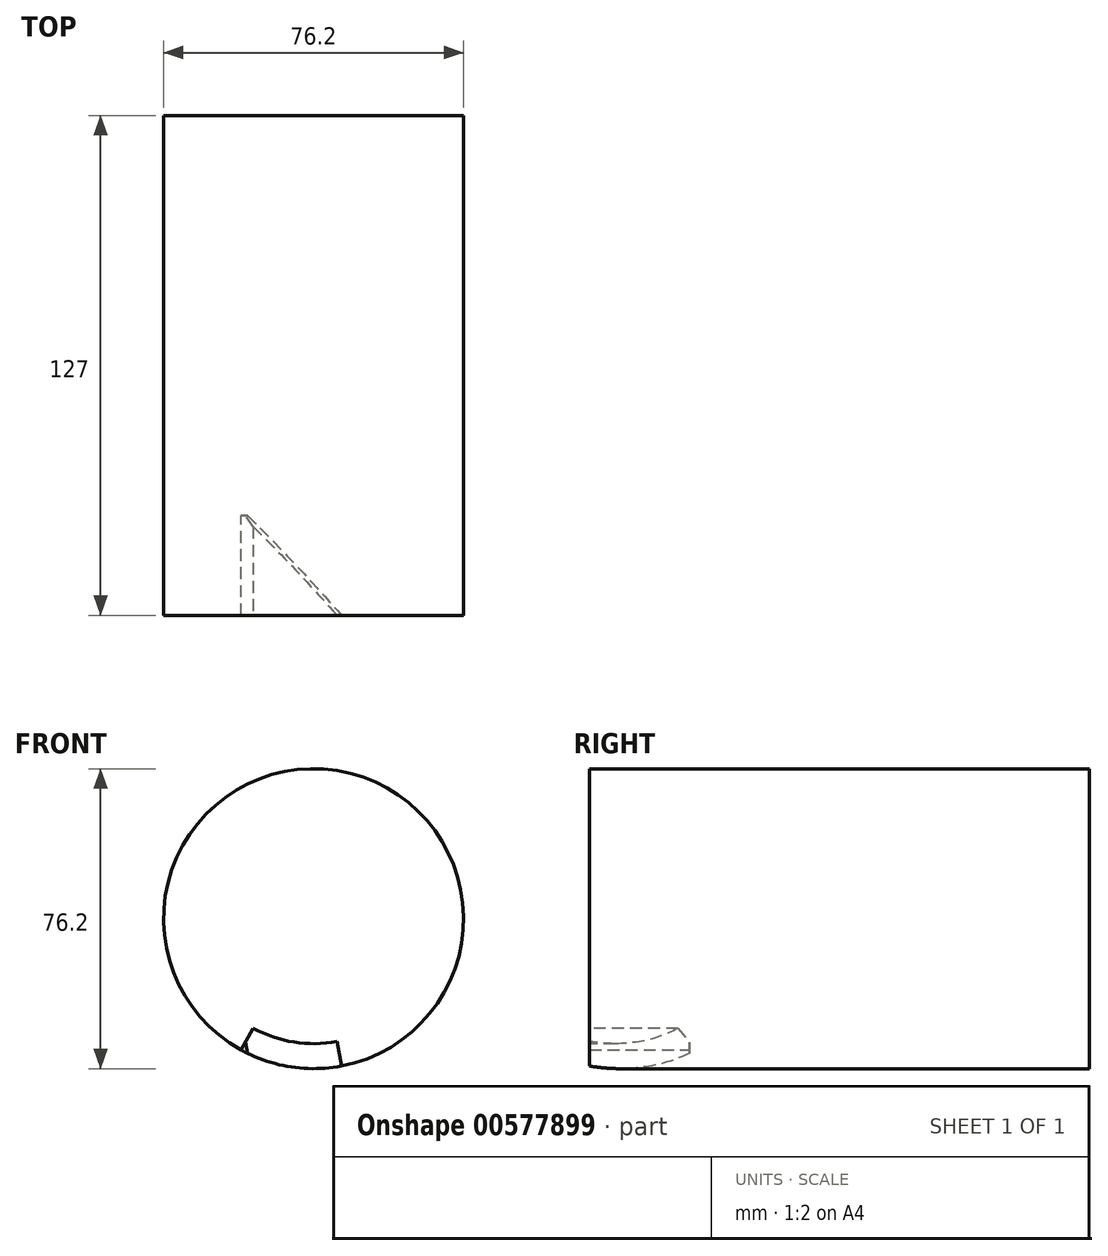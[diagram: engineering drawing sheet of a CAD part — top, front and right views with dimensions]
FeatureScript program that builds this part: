
annotation { "Feature Type Name" : "Feature", "Feature Type Description" : "" }
export const myFeature = defineFeature(function(context is Context, id is Id, definition is map)
    precondition{}
    {
        {
            var Q0;
            Q0=qCreatedBy(makeId("Front.planeOp"),FACE);
            var sketch = newSketch(context, id + "F0", { "sketchPlane" : qUnion([Q0])});
            skCircle(sketch, "E0", {"center": v(0, 0) * mm, "radius": 38.1 * mm});
            skSolve(sketch);
        }
        {
            var Q0;
            Q0 = qSketchRegion(id + "F0", true);
            extrude(context, id + "F1", {"entities" : qUnion([Q0]), "depth" : 127 * mm, "offsetDistance" : 25.4 * mm});
        }
        {
            var Q0;
            Q0=makeQuery(id+"F1.opExtrude","CAP_FACE",FACE,{"disambiguationData":[OSD([sQuery(id+"F0.wireOp",EDGE,"E0")])],"isStart":false});
            var sketch = newSketch(context, id + "F2", { "sketchPlane" : qUnion([Q0])});
            skArc(sketch, "E1", {"start": v(-15.34, -27.8) * mm, "mid": v(-5, -31.35) * mm, "end": v(5.92, -31.2) * mm});
            skArc(sketch, "E2", {"start": v(-19.94, -36.14) * mm, "mid": v(-6.5, -40.76) * mm, "end": v(7.7, -40.55) * mm});
            skLineSegment(sketch, "E3", {"start": v(-15.34, -27.8) * mm, "end": v(-19.94, -36.14) * mm});
            skLineSegment(sketch, "E4", {"start": v(5.92, -31.2) * mm, "end": v(7.7, -40.55) * mm});
            skSolve(sketch);
        }
        {
            var Q0;
            Q0 = qSketchRegion(id + "F2", true);
            extrude(context, id + "F3", {"entities" : qUnion([Q0]), "operationType" : NewBodyOperationType.REMOVE, "oppositeDirection" : true, "depth" : 25.4 * mm, "offsetDistance" : 25.4 * mm});
        }
        {
            var Q0;
            Q0=makeQuery(id+"F3.boolean.opBoolean","COPY",EDGE,{"derivedFrom":makeQuery(id+"F3.opExtrude","CAP_EDGE",EDGE,{"disambiguationData":[OSD([sQuery(id+"F2.wireOp",EDGE,"E4")])],"isStart":false})});
            chamfer(context, id + "F4", {"entities" : qUnion([Q0]), "chamferType" : ChamferType.TWO_OFFSETS, "width1" : 25.4 * mm, "oppositeDirection" : false, "width2" : 22.86 * mm, "tangentPropagation" : true});
        }
    });
